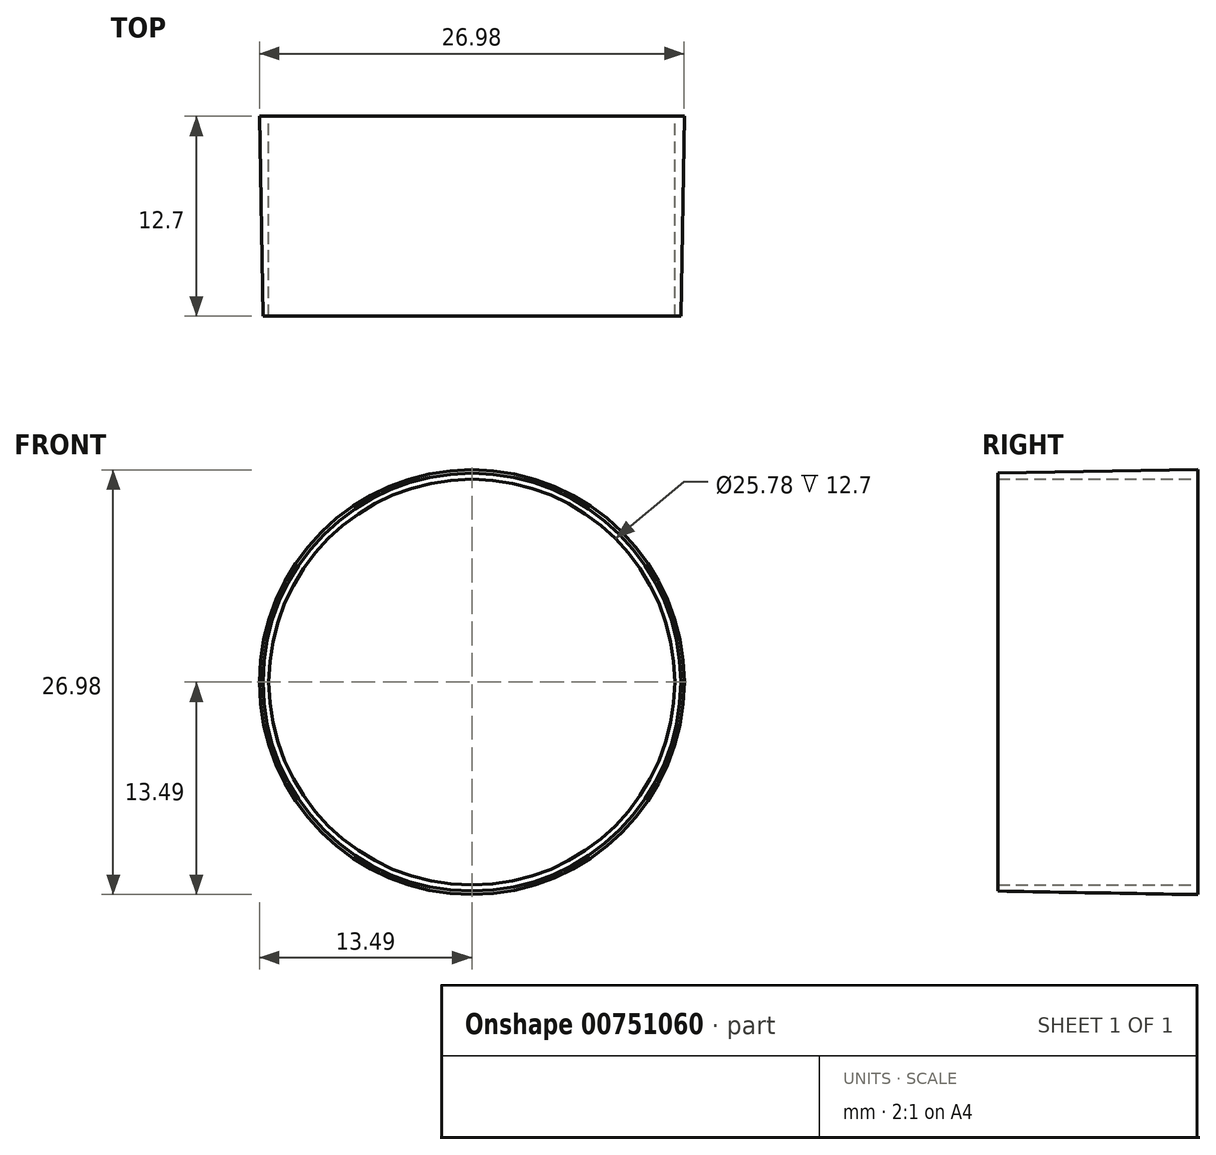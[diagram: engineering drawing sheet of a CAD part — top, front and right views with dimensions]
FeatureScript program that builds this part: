
annotation { "Feature Type Name" : "Feature", "Feature Type Description" : "" }
export const myFeature = defineFeature(function(context is Context, id is Id, definition is map)
    precondition{}
    {
        {
            var Q0;
            Q0=qCreatedBy(makeId("Front.planeOp"),FACE);
            var sketch = newSketch(context, id + "F0", { "sketchPlane" : qUnion([Q0])});
            skCircle(sketch, "E0", {"center": v(0, 0) * mm, "radius": 13.5 * mm});
            skSolve(sketch);
        }
        {
            var Q0;
            Q0=makeQuery(id+"F0.imprint","IMPRINT",FACE,{"disambiguationData":[TD([[makeQuery(id+"F0.imprint","IMPRINT",EDGE,{"derivedFrom":sQuery(id+"F0.wireOp",EDGE,"E0")}),1.0]])]});
            extrude(context, id + "F1", {"entities" : qUnion([Q0]), "depth" : 12.7 * mm, "offsetDistance" : 25.4 * mm, "hasDraft" : true, "draftAngle" : 1 * degree, "draftPullDirection" : true});
        }
        {
            var Q0;
            Q0=makeQuery(id+"F1.opExtrude","CAP_FACE",FACE,{"disambiguationData":[OSD([sQuery(id+"F0.wireOp",EDGE,"E0")])],"isStart":false});
            var sketch = newSketch(context, id + "F2", { "sketchPlane" : qUnion([Q0])});
            skSolve(sketch);
        }
        {
            var Q0;
            Q0=makeQuery(id+"F1.opExtrude","CAP_FACE",FACE,{"disambiguationData":[OSD([sQuery(id+"F0.wireOp",EDGE,"E0")])],"isStart":true});
            var sketch = newSketch(context, id + "F3", { "sketchPlane" : qUnion([Q0])});
            skCircle(sketch, "E1", {"center": v(0, 0) * mm, "radius": 12.9 * mm});
            skSolve(sketch);
        }
        {
            var Q0;
            Q0=makeQuery(id+"F3.imprint","IMPRINT",FACE,{"disambiguationData":[TD([[makeQuery(id+"F3.imprint","IMPRINT",EDGE,{"derivedFrom":sQuery(id+"F3.wireOp",EDGE,"E1")}),1.0]])]});
            var Q1;
            Q1 = qSketchRegion(id + "F3", true);
            extrude(context, id + "F4", {"entities" : qUnion([Q0, Q1]), "operationType" : NewBodyOperationType.REMOVE, "oppositeDirection" : true, "depth" : 25.4 * mm, "offsetDistance" : 25.4 * mm});
        }
    });
